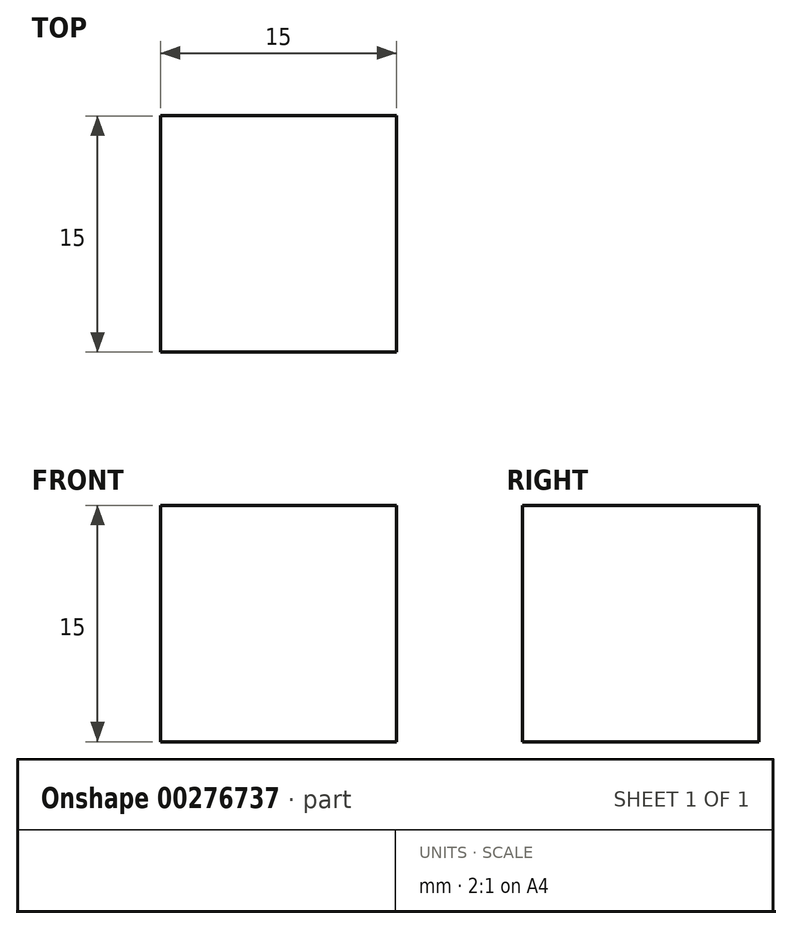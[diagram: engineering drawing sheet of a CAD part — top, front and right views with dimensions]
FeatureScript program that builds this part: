
annotation { "Feature Type Name" : "Feature", "Feature Type Description" : "" }
export const myFeature = defineFeature(function(context is Context, id is Id, definition is map)
    precondition{}
    {
        {
            var Q0;
            Q0=qCreatedBy(makeId("Top.planeOp"),FACE);
            var sketch = newSketch(context, id + "F0", { "sketchPlane" : qUnion([Q0])});
            skLineSegment(sketch, "E0.bottom", {"start": v(-5.25, 4) * mm, "end": v(9.75, 4) * mm});
            skLineSegment(sketch, "E0.top", {"start": v(-5.25, -11) * mm, "end": v(9.75, -11) * mm});
            skLineSegment(sketch, "E0.left", {"start": v(-5.25, 4) * mm, "end": v(-5.25, -11) * mm});
            skLineSegment(sketch, "E0.right", {"start": v(9.75, 4) * mm, "end": v(9.75, -11) * mm});
            skSolve(sketch);
        }
        {
            var Q0;
            Q0=makeQuery(id+"F0.imprint","IMPRINT",FACE,{"disambiguationData":[TD([[makeQuery(id+"F0.imprint","IMPRINT",EDGE,{"derivedFrom":sQuery(id+"F0.wireOp",EDGE,"E0.bottom")}),-1.0]])]});
            extrude(context, id + "F1", {"entities" : qUnion([Q0]), "depth" : 15 * mm});
        }
    });
